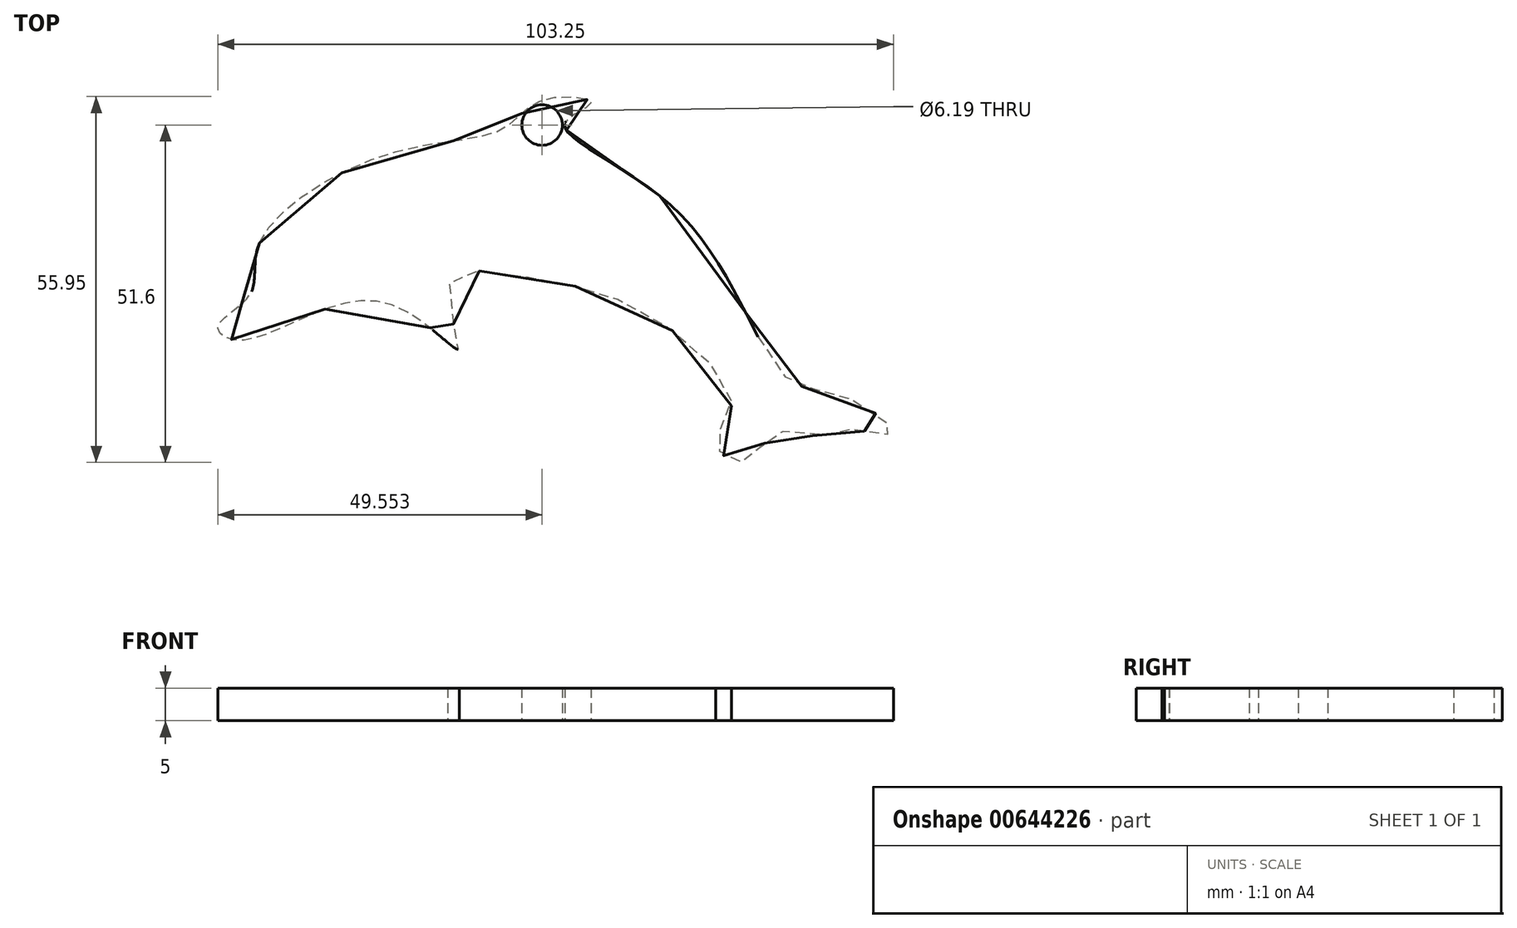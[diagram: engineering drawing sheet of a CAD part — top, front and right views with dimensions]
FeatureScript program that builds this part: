
annotation { "Feature Type Name" : "Feature", "Feature Type Description" : "" }
export const myFeature = defineFeature(function(context is Context, id is Id, definition is map)
    precondition{}
    {
        {
            var Q0;
            Q0=qCreatedBy(makeId("Top.planeOp"),FACE);
            var sketch = newSketch(context, id + "F0", { "sketchPlane" : qUnion([Q0])});
            skFitSpline(sketch, "E0", {"points": [v(-38.79, 0) * mm, v(-18.79, 13.74) * mm, v(-1.59, 17.48) * mm, v(4.77, 21.97) * mm, v(11.87, 21.4) * mm, v(7.94, 18.41) * mm, v(25.14, 4.77) * mm, v(41.78, -20.66) * mm, v(50.75, -23.46) * mm, v(58.04, -29.07) * mm, v(50.38, -28.5) * mm, v(46.64, -29.63) * mm, v(42.72, -28.5) * mm, v(37.67, -31.31) * mm, v(34.3, -33.56) * mm, v(30.94, -30.38) * mm, v(33.37, -24.58) * mm, v(19.54, -10.38) * mm, v(1.4, -5.14) * mm, v(-9.81, -6.26) * mm, v(-8.32, -16.17) * mm, v(-19.9, -9.07) * mm, v(-41.22, -14.86) * mm, v(-45.15, -12.8) * mm, v(-40.29, -7.94) * mm, v(-38.79, 0) * mm]});
            skCircle(sketch, "E1", {"center": v(4.4, 18.04) * mm, "radius": 3.1 * mm});
            skSolve(sketch);
        }
        {
            var Q0;
            Q0=makeQuery(id+"F0.imprint","IMPRINT",FACE,{"disambiguationData":[TD([[makeQuery(id+"F0.imprint","IMPRINT",EDGE,{"derivedFrom":sQuery(id+"F0.wireOp",EDGE,"E0")}),-1.0]])]});
            extrude(context, id + "F1", {"entities" : qUnion([Q0]), "depth" : 5 * mm, "offsetDistance" : 25.4 * mm});
        }
        {
            var Q0;
            Q0=sQuery(id+"F0.wireOp",EDGE,"E1");
            extrude(context, id + "F2", {"bodyType" : ToolBodyType.SURFACE, "surfaceEntities" : qUnion([Q0]), "depth" : 25 * mm, "offsetDistance" : 25 * mm});
        }
    });
